# Revit family: Practibox_S_surface_mounting_cabinet_12_modules_réf_135421_to_135434
name_source: partatom
category: Equipement électrique
revit_build: Autodesk Revit 2018 (Build: 20170223_1515(x64)
units: mm (PartAtom-declared; Revit-internal decimal feet)

## family parameters
Basée sur le plan de construction = Non
Configuration du panneau = Deux colonnes, circuits au sein
Cote de connecteur circulaire = Utiliser le diamètre
Couper avec des vides une fois chargée = Non
Numéro OmniClass = 23.80.30.11.17
Partagée = Non
Point de calcul de pièce = Non
Titre OmniClass = Distribution Boards and Control Panels
Toujours verticalement = Oui
Type d'élément = Tableau de raccordement

## types (8) — shared parameters
Fabricant = "Legrand"
"Legrand"
"Legrand"
General Conditions of Use = https://export.legrand.com
URL = www.legrand.com
depth = 210 mm  [stored 0.688976 ft]
width = 328 mm  [stored 1.07612 ft]

## per-type parameters (varying)
| type | 1R | 2R | 3R | 4R | Ina | Terminal block E | Terminal block N | door B 1 r | door B 2 r | door B 3 r | door B 4 r | door T 1 r | door T 2 r | door T 3 r | door T 4 r | door transparent | door white | height | size |
| Practibox_S_surface_mounting_cabinet_12_modules_135421 | Oui | Non | Non | Non | 63A | 10 connections Icc 6kA | 10 connections Icc 6kA | Oui | Non | Non | Non | Non | Non | Non | Non | Non | Oui | 236 mm | 1 row |
| Practibox_S_surface_mounting_cabinet_12_modules_135431 | Oui | Non | Non | Non | 63A | 10 connections Icc 6kA | 10 connections Icc 6kA | Non | Non | Non | Non | Oui | Non | Non | Non | Oui | Non | 236 mm | 1 row |
| Practibox_S_surface_mounting_cabinet_24_modules_135422 | Non | Oui | Non | Non | 90A | 18 connections Icc 6kA | 20 connections Icc 6kA | Non | Oui | Non | Non | Non | Non | Non | Non | Non | Oui | 386 mm  [stored 1.2664 ft] | 2 row |
| Practibox_S_surface_mounting_cabinet_24_modules_135432 | Non | Oui | Non | Non | 90A | 18 connections Icc 6kA | 20 connections Icc 6kA | Non | Non | Non | Non | Non | Oui | Non | Non | Oui | Non | 386 mm  [stored 1.2664 ft] | 2 row |
| Practibox_S_surface_mounting_cabinet_36_modules_135423 | Non | Non | Oui | Non | 90A | 28 connections Icc 6kA | 20 connections Icc 6kA | Non | Non | Oui | Non | Non | Non | Non | Non | Non | Oui | 536 mm | 3 row |
| Practibox_S_surface_mounting_cabinet_36_modules_135433 | Non | Non | Oui | Non | 90A | 28 connections Icc 6kA | 20 connections Icc 6kA | Non | Non | Non | Non | Non | Non | Oui | Non | Oui | Non | 536 mm | 3 row |
| Practibox_S_surface_mounting_cabinet_48_modules_135424 | Non | Non | Non | Oui | 90A | 32 connections Icc 6kA | 20 connections Icc 6kA | Non | Non | Non | Oui | Non | Non | Non | Non | Non | Oui | 766 mm  [stored 2.51312 ft] | 4 row |
| Practibox_S_surface_mounting_cabinet_48_modules_135434 | Non | Non | Non | Oui | 90A | 32 connections Icc 6kA | 20 connections Icc 6kA | Non | Non | Non | Non | Non | Non | Non | Oui | Oui | Non | 766 mm  [stored 2.51312 ft] | 4 row |

note: column(s) folded — value = type name in every type: Description

note: [stored X ft] marks values corroborated as IEEE doubles in the binary element streams (Revit-internal decimal feet)
